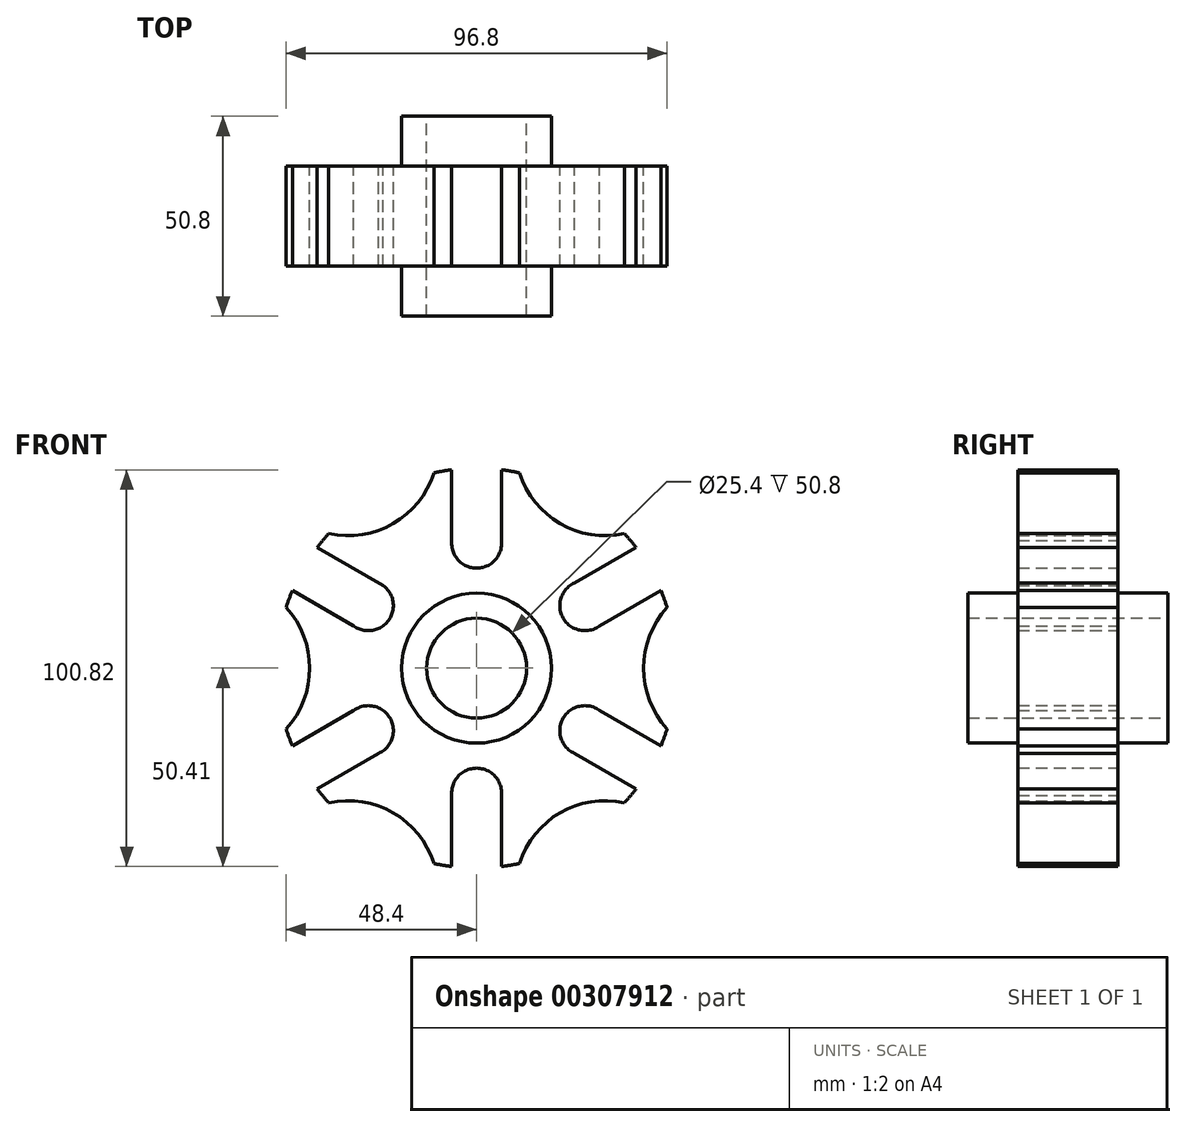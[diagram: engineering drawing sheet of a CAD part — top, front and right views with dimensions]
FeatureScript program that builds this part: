
annotation { "Feature Type Name" : "Feature", "Feature Type Description" : "" }
export const myFeature = defineFeature(function(context is Context, id is Id, definition is map)
    precondition{}
    {
        {
            var Q0;
            Q0=qCreatedBy(makeId("Front.planeOp"),FACE);
            var sketch = newSketch(context, id + "F0", { "sketchPlane" : qUnion([Q0])});
            skArc(sketch, "E0", {"start": v(48.4, 15.42) * mm, "mid": v(47.66, 17.6) * mm, "end": v(46.81, 19.73) * mm});
            skCircle(sketch, "E1", {"center": v(0, 0) * mm, "radius": 12.7 * mm});
            skCircle(sketch, "E2", {"center": v(0, 0) * mm, "radius": 19.05 * mm});
            skCircle(sketch, "E3", {"center": v(0, 0) * mm, "radius": 31.75 * mm, "construction": true});
            skLineSegment(sketch, "E4", {"start": v(0, 0) * mm, "end": v(0, -50.8) * mm, "construction": true});
            skArc(sketch, "E5", {"start": v(6.32, -32.38) * mm, "mid": v(0, -25.4) * mm, "end": v(-6.32, -32.38) * mm});
            skLineSegment(sketch, "E6", {"start": v(-6.32, -31.12) * mm, "end": v(-6.32, -50.4) * mm});
            skLineSegment(sketch, "E7", {"start": v(6.32, -31.12) * mm, "end": v(6.32, -50.4) * mm});
            skLineSegment(sketch, "E8", {"start": v(0, 0) * mm, "end": v(-50.8, 0) * mm, "construction": true});
            skLineSegment(sketch, "E9", {"start": v(0, 0) * mm, "end": v(42.42, 0) * mm});
            skLineSegment(sketch, "E10", {"start": v(0, 0) * mm, "end": v(0, 50.8) * mm, "construction": true});
            skLineSegment(sketch, "E11.MirrorCS", {"start": v(-6.32, 31.12) * mm, "end": v(-6.32, 50.4) * mm});
            skLineSegment(sketch, "E12.MirrorCS", {"start": v(6.32, 31.12) * mm, "end": v(6.32, 50.4) * mm});
            skArc(sketch, "E13.MirrorC", {"start": v(6.32, 32.38) * mm, "mid": v(0, 25.4) * mm, "end": v(-6.32, 32.38) * mm});
            skLineSegment(sketch, "E14", {"start": v(0, 0) * mm, "end": v(-44, 25.4) * mm, "construction": true});
            skLineSegment(sketch, "E15", {"start": v(0, 0) * mm, "end": v(-44, -25.4) * mm, "construction": true});
            skLineSegment(sketch, "E16", {"start": v(0, 0) * mm, "end": v(44, -25.4) * mm, "construction": true});
            skLineSegment(sketch, "E17", {"start": v(0, 0) * mm, "end": v(44, 25.4) * mm, "construction": true});
            skLineSegment(sketch, "E18.1.0", {"start": v(-23.79, -21.03) * mm, "end": v(-40.5, -30.67) * mm});
            skArc(sketch, "E18.1.1", {"start": v(-31.2, -10.72) * mm, "mid": v(-22, -12.7) * mm, "end": v(-24.89, -21.66) * mm});
            skLineSegment(sketch, "E18.1.2", {"start": v(-30.1, -10.09) * mm, "end": v(-46.81, -19.73) * mm});
            skLineSegment(sketch, "E18.2.0", {"start": v(30.1, -10.09) * mm, "end": v(46.81, -19.73) * mm});
            skArc(sketch, "E18.2.1", {"start": v(24.89, -21.66) * mm, "mid": v(22, -12.7) * mm, "end": v(31.2, -10.72) * mm});
            skLineSegment(sketch, "E18.2.2", {"start": v(23.79, -21.03) * mm, "end": v(40.5, -30.67) * mm});
            skLineSegment(sketch, "E19.1.0", {"start": v(30.1, 10.09) * mm, "end": v(46.81, 19.73) * mm});
            skArc(sketch, "E19.1.1", {"start": v(24.89, 21.66) * mm, "mid": v(22, 12.7) * mm, "end": v(31.2, 10.72) * mm});
            skLineSegment(sketch, "E19.1.2", {"start": v(23.79, 21.03) * mm, "end": v(40.5, 30.67) * mm});
            skLineSegment(sketch, "E19.2.0", {"start": v(-23.79, 21.03) * mm, "end": v(-40.5, 30.67) * mm});
            skArc(sketch, "E19.2.1", {"start": v(-31.2, 10.72) * mm, "mid": v(-22.34, 12.17) * mm, "end": v(-23.79, 21.03) * mm});
            skLineSegment(sketch, "E19.2.2", {"start": v(-30.1, 10.09) * mm, "end": v(-46.81, 19.73) * mm});
            skLineSegment(sketch, "E20", {"start": v(0, 0) * mm, "end": v(0, 3.94) * mm});
            skLineSegment(sketch, "E21", {"start": v(0, 0) * mm, "end": v(-39.62, 68.63) * mm, "construction": true});
            skLineSegment(sketch, "E22", {"start": v(0, 0) * mm, "end": v(-45.67, -79.1) * mm, "construction": true});
            skLineSegment(sketch, "E23", {"start": v(0, 0) * mm, "end": v(44.97, -77.9) * mm});
            skArc(sketch, "E24", {"start": v(37.56, -34.2) * mm, "mid": v(21.2, -36.74) * mm, "end": v(10.85, -49.63) * mm});
            skArc(sketch, "E25", {"start": v(-10.85, -49.63) * mm, "mid": v(-21.2, -36.74) * mm, "end": v(-37.56, -34.2) * mm});
            skArc(sketch, "E26", {"start": v(-48.4, -15.42) * mm, "mid": v(-42.42, 0) * mm, "end": v(-48.4, 15.42) * mm});
            skArc(sketch, "E27", {"start": v(-37.56, 34.2) * mm, "mid": v(-21.2, 36.74) * mm, "end": v(-10.85, 49.63) * mm});
            skArc(sketch, "E28", {"start": v(10.85, 49.63) * mm, "mid": v(21.2, 36.74) * mm, "end": v(37.56, 34.2) * mm});
            skArc(sketch, "E29", {"start": v(48.4, 15.42) * mm, "mid": v(42.42, 0) * mm, "end": v(48.4, -15.42) * mm});
            skArc(sketch, "E30.trimOffspring", {"start": v(10.85, 49.63) * mm, "mid": v(8.6, 50.07) * mm, "end": v(6.32, 50.4) * mm});
            skArc(sketch, "E31.trimOffspring", {"start": v(-37.56, 34.2) * mm, "mid": v(-39.06, 32.47) * mm, "end": v(-40.5, 30.67) * mm});
            skArc(sketch, "E32.trimOffspring", {"start": v(-48.4, -15.42) * mm, "mid": v(-47.66, -17.6) * mm, "end": v(-46.81, -19.73) * mm});
            skArc(sketch, "E33.trimOffspring", {"start": v(-10.85, -49.63) * mm, "mid": v(-8.6, -50.07) * mm, "end": v(-6.32, -50.4) * mm});
            skArc(sketch, "E34.trimOffspring", {"start": v(37.56, -34.2) * mm, "mid": v(39.06, -32.47) * mm, "end": v(40.5, -30.67) * mm});
            skArc(sketch, "E35.trimOffspring", {"start": v(-40.5, -30.67) * mm, "mid": v(-39.06, -32.47) * mm, "end": v(-37.56, -34.2) * mm});
            skArc(sketch, "E36.trimOffspring", {"start": v(-46.81, 19.73) * mm, "mid": v(-47.66, 17.6) * mm, "end": v(-48.4, 15.42) * mm});
            skArc(sketch, "E37.trimOffspring", {"start": v(-6.32, 50.4) * mm, "mid": v(-8.6, 50.07) * mm, "end": v(-10.85, 49.63) * mm});
            skArc(sketch, "E38.trimOffspring", {"start": v(40.5, 30.67) * mm, "mid": v(39.06, 32.47) * mm, "end": v(37.56, 34.2) * mm});
            skArc(sketch, "E39.trimOffspring", {"start": v(46.81, -19.73) * mm, "mid": v(47.66, -17.6) * mm, "end": v(48.4, -15.42) * mm});
            skArc(sketch, "E40.trimOffspring", {"start": v(6.32, -50.4) * mm, "mid": v(8.6, -50.07) * mm, "end": v(10.85, -49.63) * mm});
            skSolve(sketch);
        }
        {
            var Q0;
            {var subQ35=sQuery(id+"F0.wireOp",EDGE,"E0");Q0=makeQuery(id+"F0.imprint","IMPRINT",FACE,{"disambiguationData":[TD([[makeQuery(id+"F0.imprint","IMPRINT",EDGE,{"derivedFrom":subQ35}),1.0]])]});}
            var Q1;
            {var subQ0=sQuery(id+"F0.wireOp",EDGE,"E34.trimOffspring");Q1=makeQuery(id+"F0.imprint","IMPRINT",FACE,{"disambiguationData":[TD([[makeQuery(id+"F0.imprint","IMPRINT",EDGE,{"derivedFrom":subQ0}),1.0]])]});}
            extrude(context, id + "F1", {"entities" : qUnion([Q0, Q1]), "endBound" : BoundingType.SYMMETRIC, "depth" : 25.4 * mm});
        }
        {
            var Q0;
            {var subQ0=sQuery(id+"F0.wireOp",EDGE,"E9");var subQ1=sQuery(id+"F0.wireOp",EDGE,"E1");var subQ2=makeQuery(id+"F0.imprint","INTERSECT",VERTEX,{"derivedFrom":[subQ1,subQ0]});Q0=makeQuery(id+"F0.imprint","IMPRINT",FACE,{"disambiguationData":[TD([[makeQuery(id+"F0.imprint","IMPRINT",EDGE,{"disambiguationData":[TD([[subQ2,-1.0]])],"derivedFrom":subQ1}),-1.0]])]});}
            var Q1;
            {var subQ0=sQuery(id+"F0.wireOp",EDGE,"E9");var subQ1=sQuery(id+"F0.wireOp",EDGE,"E1");var subQ2=makeQuery(id+"F0.imprint","INTERSECT",VERTEX,{"derivedFrom":[subQ1,subQ0]});Q1=makeQuery(id+"F0.imprint","IMPRINT",FACE,{"disambiguationData":[TD([[makeQuery(id+"F0.imprint","IMPRINT",EDGE,{"disambiguationData":[TD([[subQ2,1.0]])],"derivedFrom":subQ1}),-1.0]])]});}
            extrude(context, id + "F2", {"entities" : qUnion([Q0, Q1]), "operationType" : NewBodyOperationType.ADD, "endBound" : BoundingType.SYMMETRIC, "depth" : 50.8 * mm});
        }
    });
